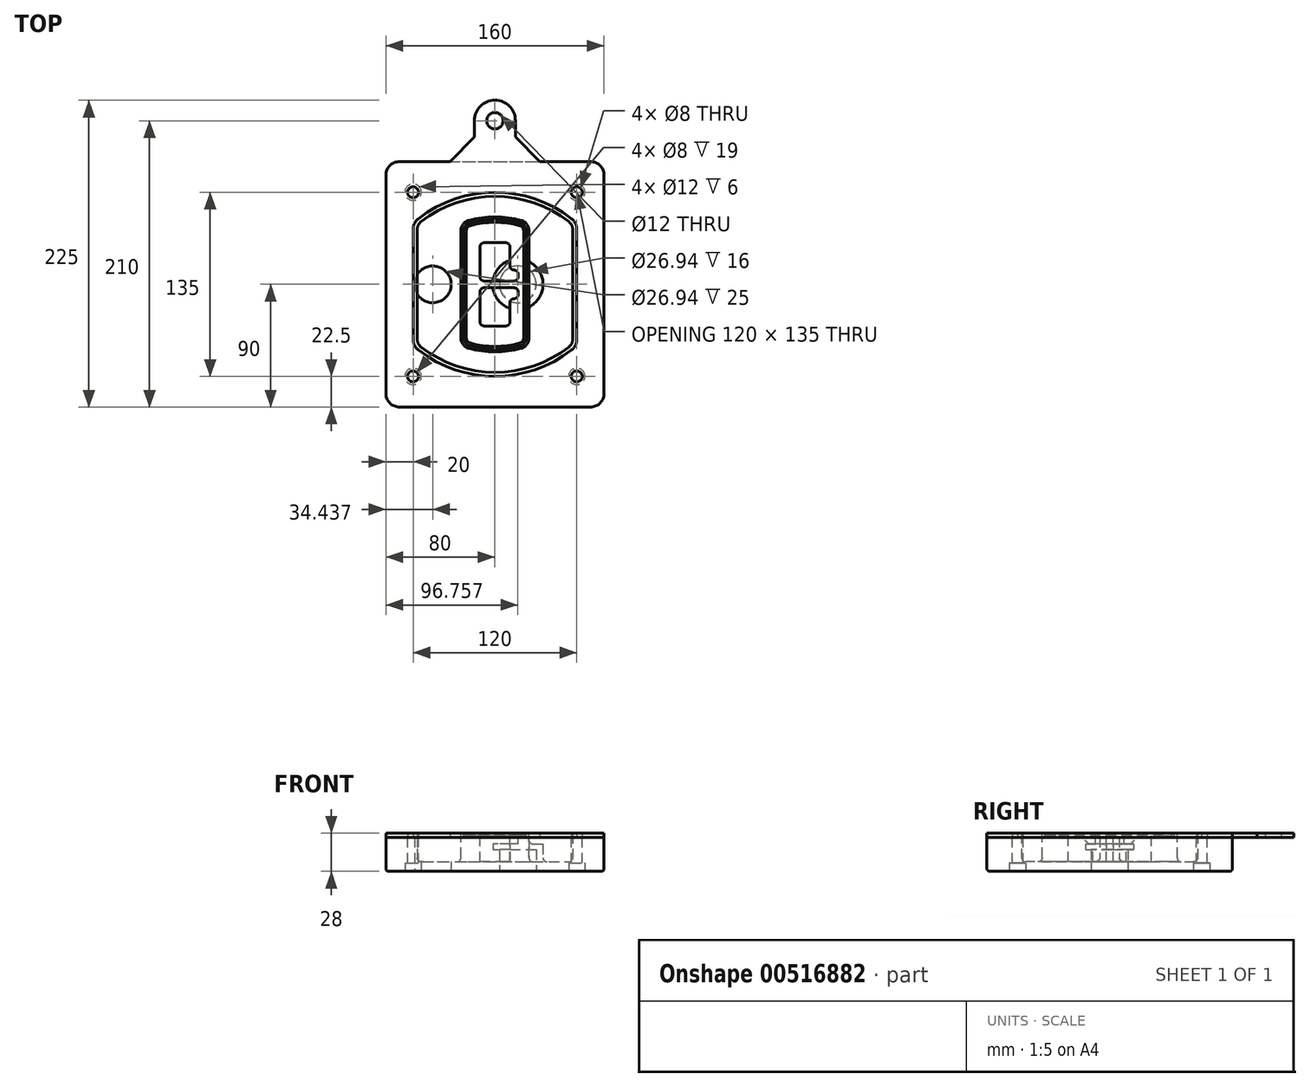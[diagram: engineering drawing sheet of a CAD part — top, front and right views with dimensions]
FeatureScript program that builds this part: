
annotation { "Feature Type Name" : "Feature", "Feature Type Description" : "" }
export const myFeature = defineFeature(function(context is Context, id is Id, definition is map)
    precondition{}
    {
        {
            var Q0;
            Q0=qCreatedBy(makeId("Top.planeOp"),FACE);
            var sketch = newSketch(context, id + "F0", { "sketchPlane" : qUnion([Q0])});
            skPoint(sketch, "E0.rect.middle", {"position": v(0, 0) * mm});
            skLineSegment(sketch, "E1.bottom", {"start": v(-70, -90) * mm, "end": v(70, -90) * mm});
            skLineSegment(sketch, "E1.top", {"start": v(-70, 90) * mm, "end": v(70, 90) * mm});
            skLineSegment(sketch, "E1.left", {"start": v(-80, -80) * mm, "end": v(-80, 80) * mm});
            skLineSegment(sketch, "E1.right", {"start": v(80, -80) * mm, "end": v(80, 80) * mm});
            skLineSegment(sketch, "E2", {"start": v(-80, 90) * mm, "end": v(80, -90) * mm, "construction": true});
            skLineSegment(sketch, "E3", {"start": v(80, 90) * mm, "end": v(-80, -90) * mm, "construction": true});
            skCircle(sketch, "E4", {"center": v(-60, 67.5) * mm, "radius": 4 * mm});
            skCircle(sketch, "E5", {"center": v(60, 67.5) * mm, "radius": 4 * mm});
            skCircle(sketch, "E6", {"center": v(60, -67.5) * mm, "radius": 4 * mm});
            skCircle(sketch, "E7", {"center": v(-60, -67.5) * mm, "radius": 4 * mm});
            skLineSegment(sketch, "E8", {"start": v(-60, 67.5) * mm, "end": v(60, 67.5) * mm, "construction": true});
            skLineSegment(sketch, "E9", {"start": v(60, 67.5) * mm, "end": v(60, -67.5) * mm, "construction": true});
            skLineSegment(sketch, "E10", {"start": v(60, -67.5) * mm, "end": v(-60, -67.5) * mm, "construction": true});
            skLineSegment(sketch, "E11", {"start": v(-60, -67.5) * mm, "end": v(-60, 67.5) * mm, "construction": true});
            skLineSegment(sketch, "E12", {"start": v(-60, 40.3) * mm, "end": v(-60, -40.3) * mm});
            skLineSegment(sketch, "E13", {"start": v(60, 40.3) * mm, "end": v(60, -40.3) * mm});
            skArc(sketch, "E14", {"start": v(56.15, 48.18) * mm, "mid": v(0, 67.5) * mm, "end": v(-56.15, 48.18) * mm});
            skArc(sketch, "E15", {"start": v(-56.15, -48.18) * mm, "mid": v(0, -67.5) * mm, "end": v(56.15, -48.18) * mm});
            skLineSegment(sketch, "E16", {"start": v(-60, 0) * mm, "end": v(60, 0) * mm, "construction": true});
            skPoint(sketch, "E17.visualSharp", {"position": v(-60, -45) * mm});
            skArc(sketch, "E17.filletArc", {"start": v(-60, -40.3) * mm, "mid": v(-58.99, -44.68) * mm, "end": v(-56.15, -48.18) * mm});
            skPoint(sketch, "E18.visualSharp", {"position": v(-60, 45) * mm});
            skArc(sketch, "E18.filletArc", {"start": v(-56.15, 48.18) * mm, "mid": v(-58.99, 44.68) * mm, "end": v(-60, 40.3) * mm});
            skPoint(sketch, "E19.visualSharp", {"position": v(60, 45) * mm});
            skArc(sketch, "E19.filletArc", {"start": v(60, 40.3) * mm, "mid": v(58.99, 44.68) * mm, "end": v(56.15, 48.18) * mm});
            skPoint(sketch, "E20.visualSharp", {"position": v(60, -45) * mm});
            skArc(sketch, "E20.filletArc", {"start": v(56.15, -48.18) * mm, "mid": v(58.99, -44.68) * mm, "end": v(60, -40.3) * mm});
            skPoint(sketch, "E21.visualSharp", {"position": v(-80, 90) * mm});
            skArc(sketch, "E21.filletArc", {"start": v(-70, 90) * mm, "mid": v(-77.07, 87.07) * mm, "end": v(-80, 80) * mm});
            skPoint(sketch, "E22.visualSharp", {"position": v(80, 90) * mm});
            skArc(sketch, "E22.filletArc", {"start": v(80, 80) * mm, "mid": v(77.07, 87.07) * mm, "end": v(70, 90) * mm});
            skPoint(sketch, "E23.visualSharp", {"position": v(80, -90) * mm});
            skArc(sketch, "E23.filletArc", {"start": v(70, -90) * mm, "mid": v(77.07, -87.07) * mm, "end": v(80, -80) * mm});
            skPoint(sketch, "E24.visualSharp", {"position": v(-80, -90) * mm});
            skArc(sketch, "E24.filletArc", {"start": v(-80, -80) * mm, "mid": v(-77.07, -87.07) * mm, "end": v(-70, -90) * mm});
            skArc(sketch, "E25.0", {"start": v(57, 40.3) * mm, "mid": v(56.3, 43.36) * mm, "end": v(54.3, 45.81) * mm});
            skLineSegment(sketch, "E25.1", {"start": v(57, 40.3) * mm, "end": v(57, -40.3) * mm});
            skArc(sketch, "E25.2", {"start": v(54.3, -45.81) * mm, "mid": v(56.3, -43.36) * mm, "end": v(57, -40.3) * mm});
            skArc(sketch, "E25.3", {"start": v(-54.3, -45.81) * mm, "mid": v(0, -64.5) * mm, "end": v(54.3, -45.81) * mm});
            skArc(sketch, "E25.4", {"start": v(-57, -40.3) * mm, "mid": v(-56.3, -43.36) * mm, "end": v(-54.3, -45.81) * mm});
            skArc(sketch, "E25.5", {"start": v(54.3, 45.81) * mm, "mid": v(0, 64.5) * mm, "end": v(-54.3, 45.81) * mm});
            skLineSegment(sketch, "E25.6", {"start": v(-57, 40.3) * mm, "end": v(-57, -40.3) * mm});
            skArc(sketch, "E25.7", {"start": v(-54.3, 45.81) * mm, "mid": v(-56.3, 43.36) * mm, "end": v(-57, 40.3) * mm});
            skArc(sketch, "E26.0", {"start": v(-58.62, 51.33) * mm, "mid": v(-62.58, 46.43) * mm, "end": v(-64, 40.3) * mm});
            skArc(sketch, "E26.1", {"start": v(58.62, 51.33) * mm, "mid": v(0, 71.5) * mm, "end": v(-58.62, 51.33) * mm});
            skArc(sketch, "E26.2", {"start": v(64, 40.3) * mm, "mid": v(62.58, 46.43) * mm, "end": v(58.62, 51.33) * mm});
            skLineSegment(sketch, "E26.3", {"start": v(64, 40.3) * mm, "end": v(64, -40.3) * mm});
            skArc(sketch, "E26.4", {"start": v(58.62, -51.33) * mm, "mid": v(62.58, -46.43) * mm, "end": v(64, -40.3) * mm});
            skLineSegment(sketch, "E26.5", {"start": v(-64, 40.3) * mm, "end": v(-64, -40.3) * mm});
            skArc(sketch, "E26.6", {"start": v(-58.62, -51.33) * mm, "mid": v(0, -71.5) * mm, "end": v(58.62, -51.33) * mm});
            skArc(sketch, "E26.7", {"start": v(-64, -40.3) * mm, "mid": v(-62.58, -46.43) * mm, "end": v(-58.62, -51.33) * mm});
            skSolve(sketch);
        }
        {
            var Q0;
            Q0=makeQuery(id+"F0.imprint","IMPRINT",FACE,{"disambiguationData":[TD([[makeQuery(id+"F0.imprint","IMPRINT",EDGE,{"derivedFrom":sQuery(id+"F0.wireOp",EDGE,"E1.bottom")}),1.0]])]});
            var Q1;
            Q1=makeQuery(id+"F0.imprint","IMPRINT",FACE,{"disambiguationData":[TD([[makeQuery(id+"F0.imprint","IMPRINT",EDGE,{"derivedFrom":sQuery(id+"F0.wireOp",EDGE,"E12")}),1.0]])]});
            var Q2;
            Q2=makeQuery(id+"F0.imprint","IMPRINT",FACE,{"disambiguationData":[TD([[makeQuery(id+"F0.imprint","IMPRINT",EDGE,{"derivedFrom":sQuery(id+"F0.wireOp",EDGE,"E25.0")}),1.0]])]});
            var Q3;
            Q3=makeQuery(id+"F0.imprint","IMPRINT",FACE,{"disambiguationData":[TD([[makeQuery(id+"F0.imprint","IMPRINT",EDGE,{"derivedFrom":sQuery(id+"F0.wireOp",EDGE,"E12")}),-1.0]])]});
            extrude(context, id + "F1", {"entities" : qUnion([Q0, Q1, Q2, Q3]), "oppositeDirection" : true, "depth" : 25 * mm});
        }
        {
            var Q0;
            Q0=makeQuery(id+"F0.imprint","IMPRINT",FACE,{"disambiguationData":[TD([[makeQuery(id+"F0.imprint","IMPRINT",EDGE,{"derivedFrom":sQuery(id+"F0.wireOp",EDGE,"E12")}),1.0]])]});
            extrude(context, id + "F2", {"entities" : qUnion([Q0]), "operationType" : NewBodyOperationType.ADD, "depth" : 3 * mm});
        }
        {
            var Q0;
            Q0=makeQuery(id+"F0.imprint","IMPRINT",FACE,{"disambiguationData":[TD([[makeQuery(id+"F0.imprint","IMPRINT",EDGE,{"derivedFrom":sQuery(id+"F0.wireOp",EDGE,"E25.0")}),1.0]])]});
            extrude(context, id + "F3", {"entities" : qUnion([Q0]), "operationType" : NewBodyOperationType.REMOVE, "oppositeDirection" : true, "depth" : 18 * mm});
        }
        {
            var Q0;
            Q0=makeQuery(id+"F2.opExtrude","CAP_FACE",FACE,{"disambiguationData":[OSD([sQuery(id+"F0.wireOp",EDGE,"E12"),sQuery(id+"F0.wireOp",EDGE,"E13"),sQuery(id+"F0.wireOp",EDGE,"E14"),sQuery(id+"F0.wireOp",EDGE,"E15"),sQuery(id+"F0.wireOp",EDGE,"E17.filletArc"),sQuery(id+"F0.wireOp",EDGE,"E18.filletArc"),sQuery(id+"F0.wireOp",EDGE,"E19.filletArc"),sQuery(id+"F0.wireOp",EDGE,"E20.filletArc"),sQuery(id+"F0.wireOp",EDGE,"E25.0"),sQuery(id+"F0.wireOp",EDGE,"E25.1"),sQuery(id+"F0.wireOp",EDGE,"E25.2"),sQuery(id+"F0.wireOp",EDGE,"E25.3"),sQuery(id+"F0.wireOp",EDGE,"E25.4"),sQuery(id+"F0.wireOp",EDGE,"E25.5"),sQuery(id+"F0.wireOp",EDGE,"E25.6"),sQuery(id+"F0.wireOp",EDGE,"E25.7")])],"isStart":false});
            var sketch = newSketch(context, id + "F4", { "sketchPlane" : qUnion([Q0])});
            skArc(sketch, "E27.0", {"start": v(-19.08, -46.97) * mm, "mid": v(0, -49.5) * mm, "end": v(19.08, -46.97) * mm});
            skArc(sketch, "E28.0", {"start": v(19.08, 46.97) * mm, "mid": v(0, 49.5) * mm, "end": v(-19.08, 46.97) * mm});
            skLineSegment(sketch, "E29", {"start": v(-25, 39.25) * mm, "end": v(-25, -39.25) * mm});
            skLineSegment(sketch, "E30", {"start": v(25, 39.25) * mm, "end": v(25, -39.25) * mm});
            skLineSegment(sketch, "E31", {"start": v(-25, 45.1) * mm, "end": v(25, 45.1) * mm, "construction": true});
            skLineSegment(sketch, "E32", {"start": v(-25, -45.1) * mm, "end": v(25, -45.1) * mm, "construction": true});
            skPoint(sketch, "E33.visualSharp", {"position": v(-25, 45.1) * mm});
            skArc(sketch, "E33.filletArc", {"start": v(-19.08, 46.97) * mm, "mid": v(-23.35, 44.11) * mm, "end": v(-25, 39.25) * mm});
            skPoint(sketch, "E34.visualSharp", {"position": v(25, 45.1) * mm});
            skArc(sketch, "E34.filletArc", {"start": v(25, 39.25) * mm, "mid": v(23.35, 44.11) * mm, "end": v(19.08, 46.97) * mm});
            skPoint(sketch, "E35.visualSharp", {"position": v(25, -45.1) * mm});
            skArc(sketch, "E35.filletArc", {"start": v(19.08, -46.97) * mm, "mid": v(23.35, -44.11) * mm, "end": v(25, -39.25) * mm});
            skPoint(sketch, "E36.visualSharp", {"position": v(-25, -45.1) * mm});
            skArc(sketch, "E36.filletArc", {"start": v(-25, -39.25) * mm, "mid": v(-23.35, -44.11) * mm, "end": v(-19.08, -46.97) * mm});
            skArc(sketch, "E37.0", {"start": v(54.3, 45.81) * mm, "mid": v(0, 64.5) * mm, "end": v(-54.3, 45.81) * mm});
            skArc(sketch, "E37.1", {"start": v(-54.3, 45.81) * mm, "mid": v(-56.3, 43.36) * mm, "end": v(-57, 40.3) * mm});
            skLineSegment(sketch, "E37.2", {"start": v(-57, 40.3) * mm, "end": v(-57, -40.3) * mm});
            skArc(sketch, "E37.3", {"start": v(-57, -40.3) * mm, "mid": v(-56.3, -43.36) * mm, "end": v(-54.3, -45.81) * mm});
            skArc(sketch, "E37.4", {"start": v(-54.3, -45.81) * mm, "mid": v(0, -64.5) * mm, "end": v(54.3, -45.81) * mm});
            skArc(sketch, "E37.5", {"start": v(54.3, -45.81) * mm, "mid": v(56.3, -43.36) * mm, "end": v(57, -40.3) * mm});
            skLineSegment(sketch, "E37.6", {"start": v(57, 40.3) * mm, "end": v(57, -40.3) * mm});
            skArc(sketch, "E37.7", {"start": v(57, 40.3) * mm, "mid": v(56.3, 43.36) * mm, "end": v(54.3, 45.81) * mm});
            skLineSegment(sketch, "E38.0", {"start": v(23, 39.25) * mm, "end": v(23, -39.25) * mm});
            skArc(sketch, "E38.1", {"start": v(18.56, -45.04) * mm, "mid": v(21.76, -42.9) * mm, "end": v(23, -39.25) * mm});
            skArc(sketch, "E38.2", {"start": v(-18.56, -45.04) * mm, "mid": v(0, -47.5) * mm, "end": v(18.56, -45.04) * mm});
            skArc(sketch, "E38.3", {"start": v(-23, -39.25) * mm, "mid": v(-21.76, -42.9) * mm, "end": v(-18.56, -45.04) * mm});
            skLineSegment(sketch, "E38.4", {"start": v(-23, 39.25) * mm, "end": v(-23, -39.25) * mm});
            skArc(sketch, "E38.5", {"start": v(23, 39.25) * mm, "mid": v(21.76, 42.9) * mm, "end": v(18.56, 45.04) * mm});
            skArc(sketch, "E38.6", {"start": v(-18.56, 45.04) * mm, "mid": v(-21.76, 42.9) * mm, "end": v(-23, 39.25) * mm});
            skArc(sketch, "E38.7", {"start": v(18.56, 45.04) * mm, "mid": v(0, 47.5) * mm, "end": v(-18.56, 45.04) * mm});
            skArc(sketch, "E39.0", {"start": v(21, 39.25) * mm, "mid": v(20.18, 41.68) * mm, "end": v(18.04, 43.1) * mm});
            skLineSegment(sketch, "E39.1", {"start": v(21, 39.25) * mm, "end": v(21, -39.25) * mm});
            skArc(sketch, "E39.2", {"start": v(18.04, -43.1) * mm, "mid": v(20.18, -41.68) * mm, "end": v(21, -39.25) * mm});
            skArc(sketch, "E39.3", {"start": v(-18.04, -43.1) * mm, "mid": v(0, -45.5) * mm, "end": v(18.04, -43.1) * mm});
            skArc(sketch, "E39.4", {"start": v(-21, -39.25) * mm, "mid": v(-20.18, -41.68) * mm, "end": v(-18.04, -43.1) * mm});
            skArc(sketch, "E39.5", {"start": v(18.04, 43.1) * mm, "mid": v(0, 45.5) * mm, "end": v(-18.04, 43.1) * mm});
            skLineSegment(sketch, "E39.6", {"start": v(-21, 39.25) * mm, "end": v(-21, -39.25) * mm});
            skArc(sketch, "E39.7", {"start": v(-18.04, 43.1) * mm, "mid": v(-20.18, 41.68) * mm, "end": v(-21, 39.25) * mm});
            skLineSegment(sketch, "E40", {"start": v(-25, 0) * mm, "end": v(25, 0) * mm, "construction": true});
            skLineSegment(sketch, "E41", {"start": v(-11, 5.5) * mm, "end": v(-11, 27.5) * mm});
            skLineSegment(sketch, "E42", {"start": v(-8, 30.5) * mm, "end": v(8, 30.5) * mm});
            skLineSegment(sketch, "E43", {"start": v(11, 27.5) * mm, "end": v(11, 13.5) * mm});
            skLineSegment(sketch, "E44", {"start": v(14, 10.5) * mm, "end": v(14, 10.5) * mm});
            skLineSegment(sketch, "E45", {"start": v(17, 7.5) * mm, "end": v(17, 5.5) * mm});
            skLineSegment(sketch, "E46", {"start": v(14, 2.5) * mm, "end": v(-8, 2.5) * mm});
            skPoint(sketch, "E47.visualSharp", {"position": v(-11, 30.5) * mm});
            skArc(sketch, "E47.filletArc", {"start": v(-8, 30.5) * mm, "mid": v(-10.12, 29.62) * mm, "end": v(-11, 27.5) * mm});
            skPoint(sketch, "E48.visualSharp", {"position": v(11, 30.5) * mm});
            skArc(sketch, "E48.filletArc", {"start": v(11, 27.5) * mm, "mid": v(10.12, 29.62) * mm, "end": v(8, 30.5) * mm});
            skPoint(sketch, "E49.visualSharp", {"position": v(11, 10.5) * mm});
            skArc(sketch, "E49.filletArc", {"start": v(11, 13.5) * mm, "mid": v(11.88, 11.38) * mm, "end": v(14, 10.5) * mm});
            skPoint(sketch, "E50.visualSharp", {"position": v(17, 10.5) * mm});
            skArc(sketch, "E50.filletArc", {"start": v(17, 7.5) * mm, "mid": v(16.12, 9.62) * mm, "end": v(14, 10.5) * mm});
            skPoint(sketch, "E51.visualSharp", {"position": v(17, 2.5) * mm});
            skArc(sketch, "E51.filletArc", {"start": v(14, 2.5) * mm, "mid": v(16.12, 3.38) * mm, "end": v(17, 5.5) * mm});
            skPoint(sketch, "E52.visualSharp", {"position": v(-11, 2.5) * mm});
            skArc(sketch, "E52.filletArc", {"start": v(-11, 5.5) * mm, "mid": v(-10.12, 3.38) * mm, "end": v(-8, 2.5) * mm});
            skLineSegment(sketch, "E53.0.MirrorCS", {"start": v(14, -2.5) * mm, "end": v(-8, -2.5) * mm});
            skArc(sketch, "E54.0.MirrorCS", {"start": v(-11, -5.5) * mm, "mid": v(-10.12, -3.38) * mm, "end": v(-8, -2.5) * mm});
            skLineSegment(sketch, "E55.0.MirrorCS", {"start": v(-11, -5.5) * mm, "end": v(-11, -27.5) * mm});
            skArc(sketch, "E56.0.MirrorCS", {"start": v(-8, -30.5) * mm, "mid": v(-10.12, -29.62) * mm, "end": v(-11, -27.5) * mm});
            skLineSegment(sketch, "E57.0.MirrorCS", {"start": v(-8, -30.5) * mm, "end": v(8, -30.5) * mm});
            skArc(sketch, "E58.0.MirrorCS", {"start": v(11, -27.5) * mm, "mid": v(10.12, -29.62) * mm, "end": v(8, -30.5) * mm});
            skLineSegment(sketch, "E59.0.MirrorCS", {"start": v(11, -27.5) * mm, "end": v(11, -13.5) * mm});
            skArc(sketch, "E60.0.MirrorCS", {"start": v(11, -13.5) * mm, "mid": v(11.88, -11.38) * mm, "end": v(14, -10.5) * mm});
            skArc(sketch, "E61.0.MirrorCS", {"start": v(17, -7.5) * mm, "mid": v(16.12, -9.62) * mm, "end": v(14, -10.5) * mm});
            skLineSegment(sketch, "E62.0.MirrorCS", {"start": v(17, -7.5) * mm, "end": v(17, -5.5) * mm});
            skArc(sketch, "E63.0.MirrorCS", {"start": v(14, -2.5) * mm, "mid": v(16.12, -3.38) * mm, "end": v(17, -5.5) * mm});
            skSolve(sketch);
        }
        {
            var Q0;
            Q0=makeQuery(id+"F4.imprint","IMPRINT",FACE,{"disambiguationData":[TD([[makeQuery(id+"F4.imprint","IMPRINT",EDGE,{"derivedFrom":sQuery(id+"F4.wireOp",EDGE,"E27.0")}),1.0]])]});
            var Q1;
            Q1=makeQuery(id+"F4.imprint","IMPRINT",FACE,{"disambiguationData":[TD([[makeQuery(id+"F4.imprint","IMPRINT",EDGE,{"derivedFrom":sQuery(id+"F4.wireOp",EDGE,"E38.0")}),-1.0]])]});
            var Q2;
            Q2=makeQuery(id+"F4.imprint","IMPRINT",FACE,{"disambiguationData":[TD([[makeQuery(id+"F4.imprint","IMPRINT",EDGE,{"derivedFrom":sQuery(id+"F4.wireOp",EDGE,"E39.0")}),1.0]])]});
            extrude(context, id + "F5", {"entities" : qUnion([Q0, Q1, Q2]), "operationType" : NewBodyOperationType.ADD, "endBound" : BoundingType.UP_TO_NEXT, "oppositeDirection" : true, "depth" : 25 * mm});
        }
        {
            var Q0;
            Q0=makeQuery(id+"F4.imprint","IMPRINT",FACE,{"disambiguationData":[TD([[makeQuery(id+"F4.imprint","IMPRINT",EDGE,{"derivedFrom":sQuery(id+"F4.wireOp",EDGE,"E38.0")}),-1.0]])]});
            extrude(context, id + "F6", {"entities" : qUnion([Q0]), "operationType" : NewBodyOperationType.REMOVE, "oppositeDirection" : true, "depth" : 2 * mm});
        }
        {
            var Q0;
            Q0=makeQuery(id+"F1.opExtrude","CAP_FACE",FACE,{"disambiguationData":[OSD([sQuery(id+"F0.wireOp",EDGE,"E1.bottom"),sQuery(id+"F0.wireOp",EDGE,"E1.top"),sQuery(id+"F0.wireOp",EDGE,"E1.left"),sQuery(id+"F0.wireOp",EDGE,"E1.right"),sQuery(id+"F0.wireOp",EDGE,"E4"),sQuery(id+"F0.wireOp",EDGE,"E5"),sQuery(id+"F0.wireOp",EDGE,"E6"),sQuery(id+"F0.wireOp",EDGE,"E7"),sQuery(id+"F0.wireOp",EDGE,"E21.filletArc"),sQuery(id+"F0.wireOp",EDGE,"E22.filletArc"),sQuery(id+"F0.wireOp",EDGE,"E23.filletArc"),sQuery(id+"F0.wireOp",EDGE,"E24.filletArc")])],"isStart":false});
            var sketch = newSketch(context, id + "F7", { "sketchPlane" : qUnion([Q0])});
            skCircle(sketch, "E64", {"center": v(16.76, 0) * mm, "radius": 13.47 * mm});
            skCircle(sketch, "E65", {"center": v(-45.56, 0) * mm, "radius": 13.47 * mm});
            skLineSegment(sketch, "E66", {"start": v(80, 0) * mm, "end": v(-80, 0) * mm});
            skCircle(sketch, "E67", {"center": v(16.76, 0) * mm, "radius": 18.47 * mm});
            skCircle(sketch, "E68", {"center": v(60, -67.5) * mm, "radius": 6 * mm});
            skCircle(sketch, "E69", {"center": v(-60, -67.5) * mm, "radius": 6 * mm});
            skCircle(sketch, "E70", {"center": v(-60, 67.5) * mm, "radius": 6 * mm});
            skCircle(sketch, "E71", {"center": v(60, 67.5) * mm, "radius": 6 * mm});
            skSolve(sketch);
        }
        {
            var Q0;
            {var subQ1=sQuery(id+"F7.wireOp",EDGE,"E66");var subQ4=sQuery(id+"F7.wireOp",EDGE,"E64");var subQ6=makeQuery(id+"F7.imprint","INTERSECT",VERTEX,{"disambiguationData":[OD(0.0)],"derivedFrom":[subQ4,subQ1]});Q0=makeQuery(id+"F7.imprint","IMPRINT",FACE,{"disambiguationData":[TD([[makeQuery(id+"F7.imprint","IMPRINT",EDGE,{"disambiguationData":[TD([[subQ6,-1.0]])],"derivedFrom":subQ4}),-1.0]])]});}
            var Q1;
            {var subQ0=sQuery(id+"F7.wireOp",EDGE,"E66");var subQ1=sQuery(id+"F7.wireOp",EDGE,"E64");var subQ3=makeQuery(id+"F7.imprint","INTERSECT",VERTEX,{"disambiguationData":[OD(0.0)],"derivedFrom":[subQ1,subQ0]});Q1=makeQuery(id+"F7.imprint","IMPRINT",FACE,{"disambiguationData":[TD([[makeQuery(id+"F7.imprint","IMPRINT",EDGE,{"disambiguationData":[TD([[subQ3,-1.0]])],"derivedFrom":subQ1}),1.0]])]});}
            var Q2;
            {var subQ0=sQuery(id+"F7.wireOp",EDGE,"E66");var subQ1=sQuery(id+"F7.wireOp",EDGE,"E64");var subQ3=makeQuery(id+"F7.imprint","INTERSECT",VERTEX,{"disambiguationData":[OD(0.0)],"derivedFrom":[subQ1,subQ0]});Q2=makeQuery(id+"F7.imprint","IMPRINT",FACE,{"disambiguationData":[TD([[makeQuery(id+"F7.imprint","IMPRINT",EDGE,{"disambiguationData":[TD([[subQ3,1.0]])],"derivedFrom":subQ1}),1.0]])]});}
            var Q3;
            {var subQ1=sQuery(id+"F7.wireOp",EDGE,"E66");var subQ4=sQuery(id+"F7.wireOp",EDGE,"E64");var subQ6=makeQuery(id+"F7.imprint","INTERSECT",VERTEX,{"disambiguationData":[OD(0.0)],"derivedFrom":[subQ4,subQ1]});Q3=makeQuery(id+"F7.imprint","IMPRINT",FACE,{"disambiguationData":[TD([[makeQuery(id+"F7.imprint","IMPRINT",EDGE,{"disambiguationData":[TD([[subQ6,1.0]])],"derivedFrom":subQ4}),-1.0]])]});}
            extrude(context, id + "F8", {"entities" : qUnion([Q0, Q1, Q2, Q3]), "operationType" : NewBodyOperationType.ADD, "oppositeDirection" : true, "depth" : 20 * mm});
        }
        {
            var Q0;
            {var subQ0=sQuery(id+"F7.wireOp",EDGE,"E66");var subQ1=sQuery(id+"F7.wireOp",EDGE,"E64");var subQ3=makeQuery(id+"F7.imprint","INTERSECT",VERTEX,{"disambiguationData":[OD(0.0)],"derivedFrom":[subQ1,subQ0]});Q0=makeQuery(id+"F7.imprint","IMPRINT",FACE,{"disambiguationData":[TD([[makeQuery(id+"F7.imprint","IMPRINT",EDGE,{"disambiguationData":[TD([[subQ3,-1.0]])],"derivedFrom":subQ1}),1.0]])]});}
            var Q1;
            {var subQ0=sQuery(id+"F7.wireOp",EDGE,"E66");var subQ1=sQuery(id+"F7.wireOp",EDGE,"E64");var subQ3=makeQuery(id+"F7.imprint","INTERSECT",VERTEX,{"disambiguationData":[OD(0.0)],"derivedFrom":[subQ1,subQ0]});Q1=makeQuery(id+"F7.imprint","IMPRINT",FACE,{"disambiguationData":[TD([[makeQuery(id+"F7.imprint","IMPRINT",EDGE,{"disambiguationData":[TD([[subQ3,1.0]])],"derivedFrom":subQ1}),1.0]])]});}
            extrude(context, id + "F9", {"entities" : qUnion([Q0, Q1]), "operationType" : NewBodyOperationType.REMOVE, "oppositeDirection" : true, "depth" : 16 * mm});
        }
        {
            var Q0;
            {var subQ0=sQuery(id+"F7.wireOp",EDGE,"E66");var subQ1=sQuery(id+"F7.wireOp",EDGE,"E65");var subQ3=makeQuery(id+"F7.imprint","INTERSECT",VERTEX,{"disambiguationData":[OD(0.0)],"derivedFrom":[subQ1,subQ0]});Q0=makeQuery(id+"F7.imprint","IMPRINT",FACE,{"disambiguationData":[TD([[makeQuery(id+"F7.imprint","IMPRINT",EDGE,{"disambiguationData":[TD([[subQ3,-1.0]])],"derivedFrom":subQ1}),1.0]])]});}
            var Q1;
            {var subQ0=sQuery(id+"F7.wireOp",EDGE,"E66");var subQ1=sQuery(id+"F7.wireOp",EDGE,"E65");var subQ3=makeQuery(id+"F7.imprint","INTERSECT",VERTEX,{"disambiguationData":[OD(0.0)],"derivedFrom":[subQ1,subQ0]});Q1=makeQuery(id+"F7.imprint","IMPRINT",FACE,{"disambiguationData":[TD([[makeQuery(id+"F7.imprint","IMPRINT",EDGE,{"disambiguationData":[TD([[subQ3,1.0]])],"derivedFrom":subQ1}),1.0]])]});}
            extrude(context, id + "F10", {"entities" : qUnion([Q0, Q1]), "operationType" : NewBodyOperationType.REMOVE, "oppositeDirection" : true, "depth" : 25 * mm});
        }
        {
            var Q0;
            Q0=makeQuery(id+"F7.imprint","IMPRINT",FACE,{"disambiguationData":[TD([[makeQuery(id+"F7.imprint","IMPRINT",EDGE,{"derivedFrom":sQuery(id+"F7.wireOp",EDGE,"E68")}),1.0]])]});
            var Q1;
            Q1=makeQuery(id+"F7.imprint","IMPRINT",FACE,{"disambiguationData":[TD([[makeQuery(id+"F7.imprint","IMPRINT",EDGE,{"derivedFrom":makeQuery(id+"F1.opExtrude","CAP_EDGE",EDGE,{"disambiguationData":[OSD([sQuery(id+"F0.wireOp",EDGE,"E5")])],"isStart":false})}),-1.0]])]});
            var Q2;
            Q2=makeQuery(id+"F7.imprint","IMPRINT",FACE,{"disambiguationData":[TD([[makeQuery(id+"F7.imprint","IMPRINT",EDGE,{"derivedFrom":sQuery(id+"F7.wireOp",EDGE,"E69")}),1.0]])]});
            var Q3;
            Q3=makeQuery(id+"F7.imprint","IMPRINT",FACE,{"disambiguationData":[TD([[makeQuery(id+"F7.imprint","IMPRINT",EDGE,{"derivedFrom":makeQuery(id+"F1.opExtrude","CAP_EDGE",EDGE,{"disambiguationData":[OSD([sQuery(id+"F0.wireOp",EDGE,"E4")])],"isStart":false})}),-1.0]])]});
            var Q4;
            Q4=makeQuery(id+"F7.imprint","IMPRINT",FACE,{"disambiguationData":[TD([[makeQuery(id+"F7.imprint","IMPRINT",EDGE,{"derivedFrom":sQuery(id+"F7.wireOp",EDGE,"E70")}),1.0]])]});
            var Q5;
            Q5=makeQuery(id+"F7.imprint","IMPRINT",FACE,{"disambiguationData":[TD([[makeQuery(id+"F7.imprint","IMPRINT",EDGE,{"derivedFrom":makeQuery(id+"F1.opExtrude","CAP_EDGE",EDGE,{"disambiguationData":[OSD([sQuery(id+"F0.wireOp",EDGE,"E7")])],"isStart":false})}),-1.0]])]});
            var Q6;
            Q6=makeQuery(id+"F7.imprint","IMPRINT",FACE,{"disambiguationData":[TD([[makeQuery(id+"F7.imprint","IMPRINT",EDGE,{"derivedFrom":sQuery(id+"F7.wireOp",EDGE,"E71")}),1.0]])]});
            var Q7;
            Q7=makeQuery(id+"F7.imprint","IMPRINT",FACE,{"disambiguationData":[TD([[makeQuery(id+"F7.imprint","IMPRINT",EDGE,{"derivedFrom":makeQuery(id+"F1.opExtrude","CAP_EDGE",EDGE,{"disambiguationData":[OSD([sQuery(id+"F0.wireOp",EDGE,"E6")])],"isStart":false})}),-1.0]])]});
            extrude(context, id + "F11", {"entities" : qUnion([Q0, Q1, Q2, Q3, Q4, Q5, Q6, Q7]), "operationType" : NewBodyOperationType.REMOVE, "oppositeDirection" : true, "depth" : 6 * mm});
        }
        {
            var Q0;
            Q0=makeQuery(id+"F9.boolean.opBoolean","COPY",FACE,{"derivedFrom":makeQuery(id+"F9.opExtrude","CAP_FACE",FACE,{"disambiguationData":[OSD([sQuery(id+"F7.wireOp",EDGE,"E64")])],"isStart":false})});
            var sketch = newSketch(context, id + "F12", { "sketchPlane" : qUnion([Q0])});
            skArc(sketch, "E72.0", {"start": v(11, 17.55) * mm, "mid": v(2.57, 11.82) * mm, "end": v(-1.54, 2.5) * mm});
            skArc(sketch, "E72.1", {"start": v(-1.54, -2.5) * mm, "mid": v(2.57, -11.82) * mm, "end": v(11, -17.55) * mm});
            skLineSegment(sketch, "E73", {"start": v(-1.54, -2.5) * mm, "end": v(14, -2.5) * mm});
            skLineSegment(sketch, "E74.0", {"start": v(14, 2.5) * mm, "end": v(-1.54, 2.5) * mm});
            skArc(sketch, "E74.1", {"start": v(14, 2.5) * mm, "mid": v(16.12, 3.38) * mm, "end": v(17, 5.5) * mm});
            skLineSegment(sketch, "E74.2", {"start": v(17, 7.5) * mm, "end": v(17, 5.5) * mm});
            skArc(sketch, "E74.3", {"start": v(17, 7.5) * mm, "mid": v(16.12, 9.62) * mm, "end": v(14, 10.5) * mm});
            skArc(sketch, "E74.4", {"start": v(11, 13.5) * mm, "mid": v(11.88, 11.38) * mm, "end": v(14, 10.5) * mm});
            skLineSegment(sketch, "E74.5", {"start": v(11, 17.55) * mm, "end": v(11, 13.5) * mm});
            skLineSegment(sketch, "E74.7", {"start": v(14, -2.5) * mm, "end": v(-1.54, -2.5) * mm});
            skArc(sketch, "E74.8", {"start": v(14, -2.5) * mm, "mid": v(16.12, -3.38) * mm, "end": v(17, -5.5) * mm});
            skLineSegment(sketch, "E74.9", {"start": v(17, -7.5) * mm, "end": v(17, -5.5) * mm});
            skArc(sketch, "E74.10", {"start": v(17, -7.5) * mm, "mid": v(16.12, -9.62) * mm, "end": v(14, -10.5) * mm});
            skArc(sketch, "E74.11", {"start": v(11, -13.5) * mm, "mid": v(11.88, -11.38) * mm, "end": v(14, -10.5) * mm});
            skLineSegment(sketch, "E74.12", {"start": v(11, -17.55) * mm, "end": v(11, -13.5) * mm});
            skPoint(sketch, "E75.orphan", {"position": v(11, -27.5) * mm});
            skPoint(sketch, "E76.orphan", {"position": v(-8, -2.5) * mm});
            skPoint(sketch, "E77.orphan", {"position": v(-8, 2.5) * mm});
            skPoint(sketch, "E78.orphan", {"position": v(11, 27.5) * mm});
            skSolve(sketch);
        }
        {
            var Q0;
            {var subQ7=sQuery(id+"F12.wireOp",EDGE,"E72.0");var subQ14=sQuery(id+"F12.wireOp",EDGE,"E72.1");var subQ16=sQuery(id+"F12.wireOp",EDGE,"E74.1");var subQ18=sQuery(id+"F12.wireOp",EDGE,"E74.8");Q0=qUnion([makeQuery(id+"F12.imprint","IMPRINT",FACE,{"disambiguationData":[TD([[makeQuery(id+"F12.imprint","IMPRINT",EDGE,{"derivedFrom":subQ7}),1.0]])]}),makeQuery(id+"F12.imprint","IMPRINT",FACE,{"disambiguationData":[TD([[makeQuery(id+"F12.imprint","IMPRINT",EDGE,{"derivedFrom":subQ14}),1.0]])]}),makeQuery(id+"F12.imprint","IMPRINT",FACE,{"disambiguationData":[TD([[makeQuery(id+"F12.imprint","IMPRINT",EDGE,{"derivedFrom":subQ16}),1.0]])]}),makeQuery(id+"F12.imprint","IMPRINT",FACE,{"disambiguationData":[TD([[makeQuery(id+"F12.imprint","IMPRINT",EDGE,{"derivedFrom":subQ18}),-1.0]])]})]);}
            var Q1;
            Q1=makeQuery(id+"F5.boolean.opBoolean","SPLIT",FACE,{"disambiguationData":[TD([makeQuery(id+"F5.opExtrude","SWEPT_FACE",FACE,{"disambiguationData":[OSD([sQuery(id+"F4.wireOp",EDGE,"E41")])]})])],"derivedFrom":makeQuery(id+"F3.boolean.opBoolean","COPY",FACE,{"derivedFrom":makeQuery(id+"F3.opExtrude","CAP_FACE",FACE,{"disambiguationData":[OSD([sQuery(id+"F0.wireOp",EDGE,"E25.0"),sQuery(id+"F0.wireOp",EDGE,"E25.1"),sQuery(id+"F0.wireOp",EDGE,"E25.2"),sQuery(id+"F0.wireOp",EDGE,"E25.3"),sQuery(id+"F0.wireOp",EDGE,"E25.4"),sQuery(id+"F0.wireOp",EDGE,"E25.5"),sQuery(id+"F0.wireOp",EDGE,"E25.6"),sQuery(id+"F0.wireOp",EDGE,"E25.7")])],"isStart":false})})});
            extrude(context, id + "F13", {"entities" : qUnion([Q0]), "operationType" : NewBodyOperationType.REMOVE, "endBound" : BoundingType.UP_TO_SURFACE, "endBoundEntityFace" : qUnion([Q1]), "depth" : 25 * mm});
        }
        {
            var Q0;
            Q0=makeQuery(id+"F3.boolean.opBoolean","COPY",EDGE,{"derivedFrom":makeQuery(id+"F3.opExtrude","CAP_EDGE",EDGE,{"disambiguationData":[OSD([sQuery(id+"F0.wireOp",EDGE,"E25.6")])],"isStart":false})});
            var Q1;
            Q1=makeQuery(id+"F8.boolean.opBoolean","INTERSECT",EDGE,{"derivedFrom":[makeQuery(id+"F5.opExtrude","SWEPT_FACE",FACE,{"disambiguationData":[OSD([sQuery(id+"F4.wireOp",EDGE,"E30")])]}),makeQuery(id+"F8.opExtrude","CAP_FACE",FACE,{"disambiguationData":[OSD([sQuery(id+"F7.wireOp",EDGE,"E67")])],"isStart":false})]});
            var Q2;
            Q2=makeQuery(id+"F8.boolean.opBoolean","INTERSECT",EDGE,{"disambiguationData":[OD(1.0)],"derivedFrom":[makeQuery(id+"F5.opExtrude","SWEPT_FACE",FACE,{"disambiguationData":[OSD([sQuery(id+"F4.wireOp",EDGE,"E30")])]}),makeQuery(id+"F8.opExtrude","SWEPT_FACE",FACE,{"disambiguationData":[OSD([sQuery(id+"F7.wireOp",EDGE,"E67")])]})]});
            var Q3;
            {var subQ0=sQuery(id+"F4.wireOp",EDGE,"E30");Q3=makeQuery(id+"F8.boolean.opBoolean","SPLIT",EDGE,{"disambiguationData":[TD([makeQuery(id+"F5.opExtrude","SWEPT_FACE",FACE,{"disambiguationData":[OSD([sQuery(id+"F4.wireOp",EDGE,"E35.filletArc")])]})])],"derivedFrom":makeQuery(id+"F5.opExtrude","CAP_EDGE",EDGE,{"disambiguationData":[OSD([subQ0])],"isStart":false})});}
            var Q4;
            {var subQ0=sQuery(id+"F0.wireOp",EDGE,"E25.7");var subQ1=sQuery(id+"F0.wireOp",EDGE,"E25.1");var subQ2=sQuery(id+"F0.wireOp",EDGE,"E25.6");var subQ3=sQuery(id+"F0.wireOp",EDGE,"E25.5");var subQ4=sQuery(id+"F0.wireOp",EDGE,"E25.4");var subQ5=sQuery(id+"F0.wireOp",EDGE,"E25.0");var subQ6=sQuery(id+"F0.wireOp",EDGE,"E25.2");var subQ7=sQuery(id+"F0.wireOp",EDGE,"E25.3");Q4=makeQuery(id+"F8.boolean.opBoolean","INTERSECT",EDGE,{"derivedFrom":[makeQuery(id+"F5.boolean.opBoolean","SPLIT",FACE,{"disambiguationData":[TD([makeQuery(id+"F2.opExtrude","SWEPT_FACE",FACE,{"disambiguationData":[OSD([subQ5])]})])],"derivedFrom":makeQuery(id+"F3.boolean.opBoolean","COPY",FACE,{"derivedFrom":makeQuery(id+"F3.opExtrude","CAP_FACE",FACE,{"disambiguationData":[OSD([subQ5,subQ1,subQ6,subQ7,subQ4,subQ3,subQ2,subQ0])],"isStart":false})})}),makeQuery(id+"F8.opExtrude","SWEPT_FACE",FACE,{"disambiguationData":[OSD([sQuery(id+"F7.wireOp",EDGE,"E67")])]})]});}
            var Q5;
            Q5=makeQuery(id+"F8.boolean.opBoolean","INTERSECT",EDGE,{"disambiguationData":[OD(0.0)],"derivedFrom":[makeQuery(id+"F5.opExtrude","SWEPT_FACE",FACE,{"disambiguationData":[OSD([sQuery(id+"F4.wireOp",EDGE,"E30")])]}),makeQuery(id+"F8.opExtrude","SWEPT_FACE",FACE,{"disambiguationData":[OSD([sQuery(id+"F7.wireOp",EDGE,"E67")])]})]});
            fillet(context, id + "F14", {"entities" : qUnion([Q0, Q1, Q2, Q3, Q4, Q5]), "radius" : 3 * mm, "tangentPropagation" : true, "allowEdgeOverflow" : false});
        }
        {
            var Q0;
            Q0=makeQuery(id+"F1.opExtrude","CAP_EDGE",EDGE,{"disambiguationData":[OSD([sQuery(id+"F0.wireOp",EDGE,"E1.bottom")])],"isStart":false});
            fillet(context, id + "F15", {"entities" : qUnion([Q0]), "radius" : 2 * mm, "tangentPropagation" : true, "allowEdgeOverflow" : false});
        }
        {
            var Q0;
            {var subQ0=sQuery(id+"F0.wireOp",EDGE,"E21.filletArc");var subQ1=sQuery(id+"F0.wireOp",EDGE,"E7");var subQ2=sQuery(id+"F0.wireOp",EDGE,"E6");var subQ3=sQuery(id+"F0.wireOp",EDGE,"E5");var subQ4=sQuery(id+"F0.wireOp",EDGE,"E4");var subQ5=sQuery(id+"F0.wireOp",EDGE,"E22.filletArc");var subQ6=sQuery(id+"F0.wireOp",EDGE,"E1.bottom");var subQ7=sQuery(id+"F0.wireOp",EDGE,"E1.right");var subQ8=sQuery(id+"F0.wireOp",EDGE,"E1.top");var subQ9=sQuery(id+"F0.wireOp",EDGE,"E1.left");var subQ10=sQuery(id+"F0.wireOp",EDGE,"E23.filletArc");var subQ11=sQuery(id+"F0.wireOp",EDGE,"E24.filletArc");Q0=makeQuery(id+"F2.boolean.opBoolean","SPLIT",FACE,{"disambiguationData":[TD([makeQuery(id+"F1.opExtrude","SWEPT_FACE",FACE,{"disambiguationData":[OSD([subQ6])]})])],"derivedFrom":makeQuery(id+"F1.opExtrude","CAP_FACE",FACE,{"disambiguationData":[OSD([subQ6,subQ8,subQ9,subQ7,subQ4,subQ3,subQ2,subQ1,subQ0,subQ5,subQ10,subQ11])],"isStart":true})});}
            var sketch = newSketch(context, id + "F16", { "sketchPlane" : qUnion([Q0])});
            skLineSegment(sketch, "E79", {"start": v(0, 90) * mm, "end": v(0, 120) * mm, "construction": true});
            skCircle(sketch, "E80", {"center": v(0, 120) * mm, "radius": 6 * mm});
            skArc(sketch, "E81", {"start": v(15, 120) * mm, "mid": v(0, 135) * mm, "end": v(-15, 120) * mm});
            skLineSegment(sketch, "E82", {"start": v(-15, 120) * mm, "end": v(-15, 108) * mm});
            skLineSegment(sketch, "E83", {"start": v(-15, 108) * mm, "end": v(-33, 90) * mm});
            skLineSegment(sketch, "E84", {"start": v(15, 120) * mm, "end": v(15, 108) * mm});
            skLineSegment(sketch, "E85", {"start": v(15, 108) * mm, "end": v(33, 90) * mm});
            skPoint(sketch, "E86.endSnap0", {"position": v(-80, 0) * mm});
            skLineSegment(sketch, "E87", {"start": v(-84.76, 0) * mm, "end": v(95.33, 0) * mm, "construction": true});
            skPoint(sketch, "E87.startSnap0", {"position": v(-60, 0) * mm});
            skPoint(sketch, "E87.endSnap0", {"position": v(80, 0) * mm});
            skLineSegment(sketch, "E88.MirrorCS", {"start": v(0, -90) * mm, "end": v(0, -120) * mm, "construction": true});
            skArc(sketch, "E89.MirrorCS", {"start": v(15, -120) * mm, "mid": v(0, -135) * mm, "end": v(-15, -120) * mm});
            skLineSegment(sketch, "E90.MirrorCS", {"start": v(-15, -120) * mm, "end": v(-15, -108) * mm});
            skLineSegment(sketch, "E91.MirrorCS", {"start": v(15, -108) * mm, "end": v(33, -90) * mm});
            skLineSegment(sketch, "E92.MirrorCS", {"start": v(-15, -108) * mm, "end": v(-33, -90) * mm});
            skCircle(sketch, "E93.MirrorC", {"center": v(0, -120) * mm, "radius": 6 * mm});
            skLineSegment(sketch, "E94.MirrorCS", {"start": v(15, -120) * mm, "end": v(15, -108) * mm});
            skSolve(sketch);
        }
        {
            var Q0;
            Q0=makeQuery(id+"F16.imprint","IMPRINT",FACE,{"disambiguationData":[TD([[makeQuery(id+"F16.imprint","IMPRINT",EDGE,{"derivedFrom":sQuery(id+"F16.wireOp",EDGE,"E80")}),-1.0]])]});
            var Q1;
            Q1=makeQuery(id+"F16.imprint","IMPRINT",FACE,{"disambiguationData":[TD([[makeQuery(id+"F16.imprint","IMPRINT",EDGE,{"derivedFrom":sQuery(id+"F16.wireOp",EDGE,"E89.MirrorCS")}),-1.0]])]});
            var Q2;
            Q2=makeQuery(id+"F16.imprint","IMPRINT",FACE,{"disambiguationData":[TD([[makeQuery(id+"F16.imprint","IMPRINT",EDGE,{"derivedFrom":makeQuery(id+"F1.opExtrude","CAP_EDGE",EDGE,{"disambiguationData":[OSD([sQuery(id+"F0.wireOp",EDGE,"E1.left")])],"isStart":true})}),-1.0]])]});
            var Q3;
            Q3=makeQuery(id+"F2.opExtrude","CAP_FACE",FACE,{"disambiguationData":[OSD([sQuery(id+"F0.wireOp",EDGE,"E12"),sQuery(id+"F0.wireOp",EDGE,"E13"),sQuery(id+"F0.wireOp",EDGE,"E14"),sQuery(id+"F0.wireOp",EDGE,"E15"),sQuery(id+"F0.wireOp",EDGE,"E17.filletArc"),sQuery(id+"F0.wireOp",EDGE,"E18.filletArc"),sQuery(id+"F0.wireOp",EDGE,"E19.filletArc"),sQuery(id+"F0.wireOp",EDGE,"E20.filletArc"),sQuery(id+"F0.wireOp",EDGE,"E25.0"),sQuery(id+"F0.wireOp",EDGE,"E25.1"),sQuery(id+"F0.wireOp",EDGE,"E25.2"),sQuery(id+"F0.wireOp",EDGE,"E25.3"),sQuery(id+"F0.wireOp",EDGE,"E25.4"),sQuery(id+"F0.wireOp",EDGE,"E25.5"),sQuery(id+"F0.wireOp",EDGE,"E25.6"),sQuery(id+"F0.wireOp",EDGE,"E25.7")])],"isStart":false});
            extrude(context, id + "F17", {"entities" : qUnion([Q0, Q1, Q2]), "endBound" : BoundingType.UP_TO_SURFACE, "depth" : 25 * mm, "endBoundEntityFace" : qUnion([Q3]), "offsetDistance" : 25 * mm});
        }
    });
